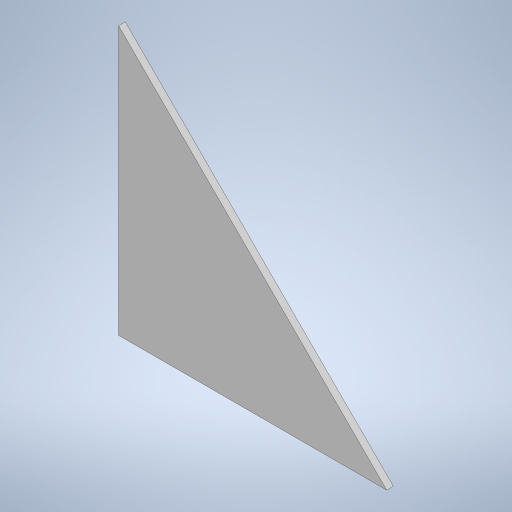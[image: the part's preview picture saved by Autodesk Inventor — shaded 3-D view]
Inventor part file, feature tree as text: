
AUTODESK INVENTOR PART (.ipt)
format: ipt  version: 2023 (Build 270158000, 158)  size: 216,576 bytes
history: native  units: mm
features: other x1, extrude x1, sketch x1
ambient origin geometry x8: Origin, YZ Plane, XZ Plane, XY Plane, X Axis, Y Axis, Z Axis, Center Point
bodies: Body1 (feature_tree)
feature tree (3):
  other  "Bryła1"
  extrude  "Wyciągnięcie proste1"  Depth=200.0mm
  sketch  "Szkic1"
